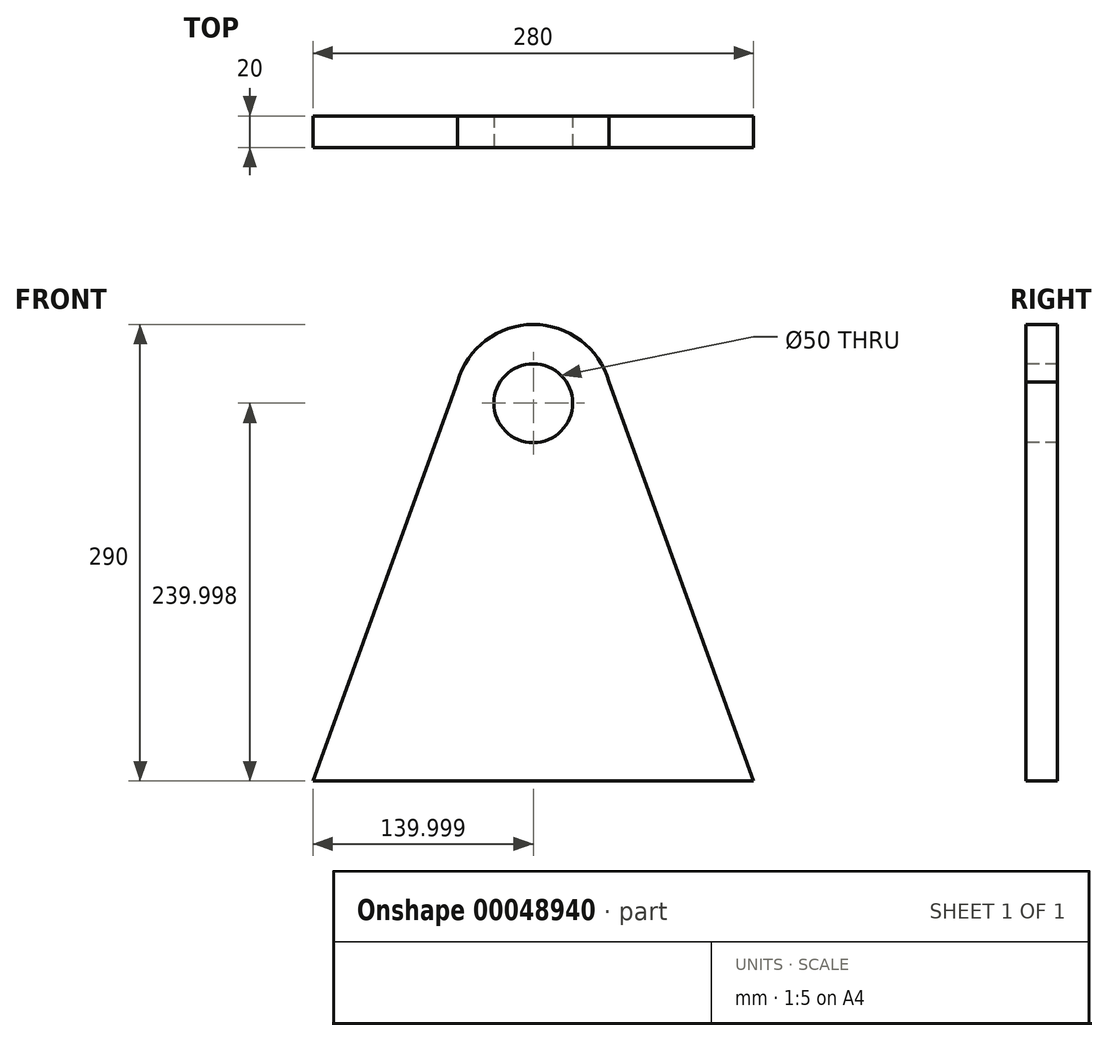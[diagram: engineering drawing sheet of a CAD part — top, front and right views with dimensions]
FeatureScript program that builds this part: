
annotation { "Feature Type Name" : "Feature", "Feature Type Description" : "" }
export const myFeature = defineFeature(function(context is Context, id is Id, definition is map)
    precondition{}
    {
        {
            var Q0;
            Q0=qCreatedBy(makeId("Front.planeOp"),FACE);
            var sketch = newSketch(context, id + "F0", { "sketchPlane" : qUnion([Q0])});
            skLineSegment(sketch, "E0", {"start": v(-180.6, -107.41) * mm, "end": v(-40.6, -107.41) * mm});
            skLineSegment(sketch, "E1", {"start": v(-40.6, -107.41) * mm, "end": v(-40.6, 132.59) * mm, "construction": true});
            skLineSegment(sketch, "E2", {"start": v(-180.6, -107.41) * mm, "end": v(-88.72, 146.16) * mm});
            skLineSegment(sketch, "E3", {"start": v(-40.6, 132.59) * mm, "end": v(-93.63, 132.59) * mm, "construction": true});
            skArc(sketch, "E4", {"start": v(-40.6, 182.59) * mm, "mid": v(-70.77, 172.45) * mm, "end": v(-88.72, 146.16) * mm});
            skLineSegment(sketch, "E5.MirrorCS", {"start": v(99.4, -107.41) * mm, "end": v(7.53, 146.16) * mm});
            skLineSegment(sketch, "E6.MirrorCS", {"start": v(99.4, -107.41) * mm, "end": v(-40.6, -107.41) * mm});
            skArc(sketch, "E7.MirrorCS", {"start": v(-40.6, 182.59) * mm, "mid": v(-10.41, 172.45) * mm, "end": v(7.53, 146.16) * mm});
            skCircle(sketch, "E8", {"center": v(-40.6, 132.59) * mm, "radius": 25 * mm});
            skSolve(sketch);
        }
        {
            var Q0;
            Q0=makeQuery(id+"F0.imprint","IMPRINT",FACE,{"disambiguationData":[TD([[makeQuery(id+"F0.imprint","IMPRINT",EDGE,{"derivedFrom":sQuery(id+"F0.wireOp",EDGE,"E0")}),1.0]])]});
            extrude(context, id + "F1", {"entities" : qUnion([Q0]), "oppositeDirection" : true, "depth" : 20 * mm});
        }
    });
